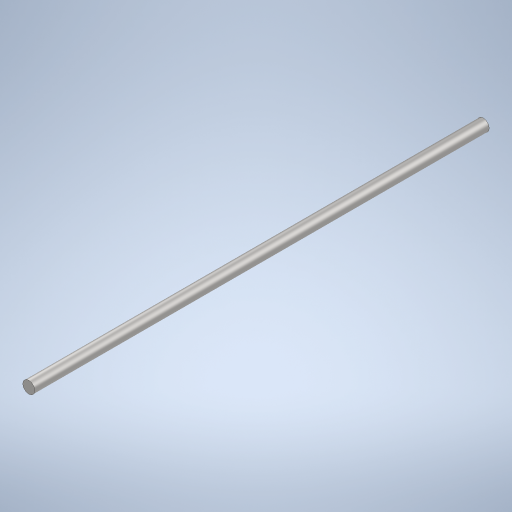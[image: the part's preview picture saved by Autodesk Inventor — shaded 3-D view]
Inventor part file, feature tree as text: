
AUTODESK INVENTOR PART (.ipt)
format: ipt  version: 2023.2 (Build 272271000, 271)  size: 259,072 bytes
history: native  units: mm
features: extrude x1, sketch x1
ambient origin geometry x8: Origin, YZ Plane, XZ Plane, XY Plane, X Axis, Y Axis, Z Axis, Center Point
bodies: Solid1 (feature_tree)
feature tree (2):
  extrude  "Extrusion1"  Depth=300.0mm TaperAngle=0.0deg
  sketch  "Sketch1"  dims[d0=8.0mm d1=300.0mm d2=0.0mm]
